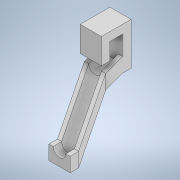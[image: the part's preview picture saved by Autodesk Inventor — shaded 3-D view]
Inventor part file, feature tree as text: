
AUTODESK INVENTOR PART (.ipt)
format: ipt  version: 2021 (Build 250183000, 183)  size: 193,536 bytes
history: native  units: mm
features: sketch x7, extrude x4, plane x2, sweep x1, loft x1, other x1
ambient origin geometry x8: Origin, YZ Plane, XZ Plane, XY Plane, X Axis, Y Axis, Z Axis, Center Point
bodies: Body1 (feature_tree)
feature tree (16):
  extrude  "Extrusion4"  Depth=50.0mm
  extrude  "Extrusion5"  Depth=10.0mm
  extrude  "Extrusion6"  Depth=10.0mm TaperAngle=0.0deg
  plane  "Work Plane1"
  plane  "Work Plane2"
  sketch  "Sketch12"  dims[d18=15.0mm d19=0.0mm d20=30.0mm]
  sweep  "Sweep2"
  loft  "Loft1"
  extrude  "Extrusion7"  Depth=5.0mm
  sketch  "Sketch5"  dims[d11=25.0mm d12=50.0mm]
  sketch  "Sketch6"  dims[d13=15.0mm d14=10.0mm]
  sketch  "Sketch7"  dims[d15=12.5mm d16=10.0mm d17=0.0mm]
  sketch  "Sketch13"  dims[d21=10.0mm d22=0.0mm d23=-12.5mm d39=90.0mm]
  sketch  "Sketch14"  dims[d48=5.0mm d49=5.0mm]
  other  "Edges1"
  sketch  "Sketch15"  dims[d50=7.5mm d51=17.0mm d55=15.0mm d56=5.0mm d57=17.0mm d58=25.0mm d62=8.5mm d63=12.217305mm d64=20.0mm d65=0.0mm d66=0.0mm d67=0.0mm d68=90.0deg d69=0.0mm d70=90.0deg d71=10.0mm d72=0.0mm]
